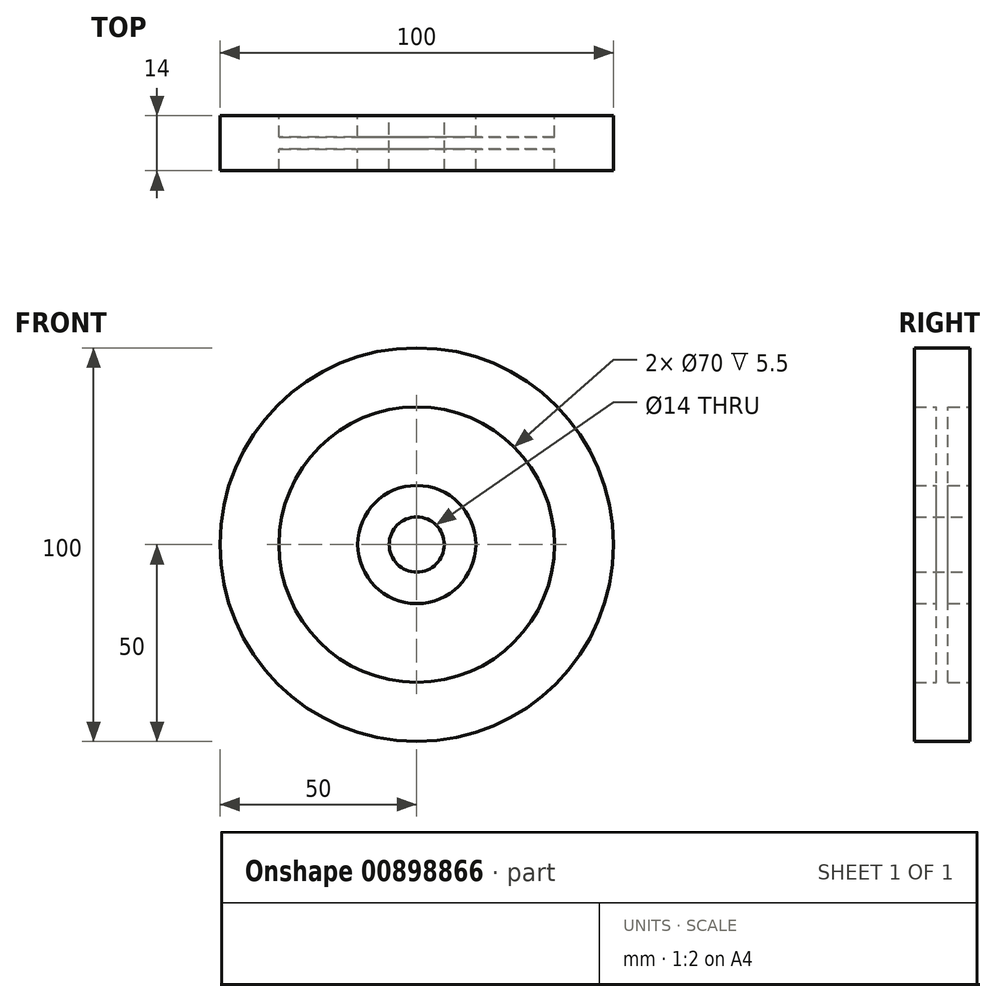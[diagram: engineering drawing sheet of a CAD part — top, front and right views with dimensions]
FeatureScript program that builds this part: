
annotation { "Feature Type Name" : "Feature", "Feature Type Description" : "" }
export const myFeature = defineFeature(function(context is Context, id is Id, definition is map)
    precondition{}
    {
        {
            var Q0;
            Q0=qCreatedBy(makeId("Front.planeOp"),FACE);
            var sketch = newSketch(context, id + "F0", { "sketchPlane" : qUnion([Q0])});
            skCircle(sketch, "E0", {"center": v(0, 0) * mm, "radius": 7 * mm});
            skCircle(sketch, "E1", {"center": v(0, 0) * mm, "radius": 15 * mm});
            skCircle(sketch, "E2", {"center": v(0, 0) * mm, "radius": 35 * mm});
            skCircle(sketch, "E3", {"center": v(0, 0) * mm, "radius": 50 * mm});
            skSolve(sketch);
        }
        {
            var Q0;
            Q0 = qSketchRegion(id + "F0", true);
            extrude(context, id + "F1", {"entities" : qUnion([Q0]), "endBound" : BoundingType.SYMMETRIC, "depth" : 14 * mm, "offsetDistance" : 25 * mm});
        }
        {
            var Q0;
            Q0=makeQuery(id+"F0.imprint","IMPRINT",FACE,{"disambiguationData":[TD([[makeQuery(id+"F0.imprint","IMPRINT",EDGE,{"derivedFrom":sQuery(id+"F0.wireOp",EDGE,"E1")}),-1.0]])]});
            extrude(context, id + "F2", {"entities" : qUnion([Q0]), "operationType" : NewBodyOperationType.ADD, "endBound" : BoundingType.SYMMETRIC, "depth" : 3 * mm, "offsetDistance" : 25 * mm});
        }
        {
            var Q0;
            Q0=makeQuery(id+"F0.imprint","IMPRINT",FACE,{"disambiguationData":[TD([[makeQuery(id+"F0.imprint","IMPRINT",EDGE,{"derivedFrom":sQuery(id+"F0.wireOp",EDGE,"E0")}),-1.0]])]});
            extrude(context, id + "F3", {"entities" : qUnion([Q0]), "operationType" : NewBodyOperationType.ADD, "endBound" : BoundingType.SYMMETRIC, "depth" : 14 * mm, "offsetDistance" : 25 * mm});
        }
    });
